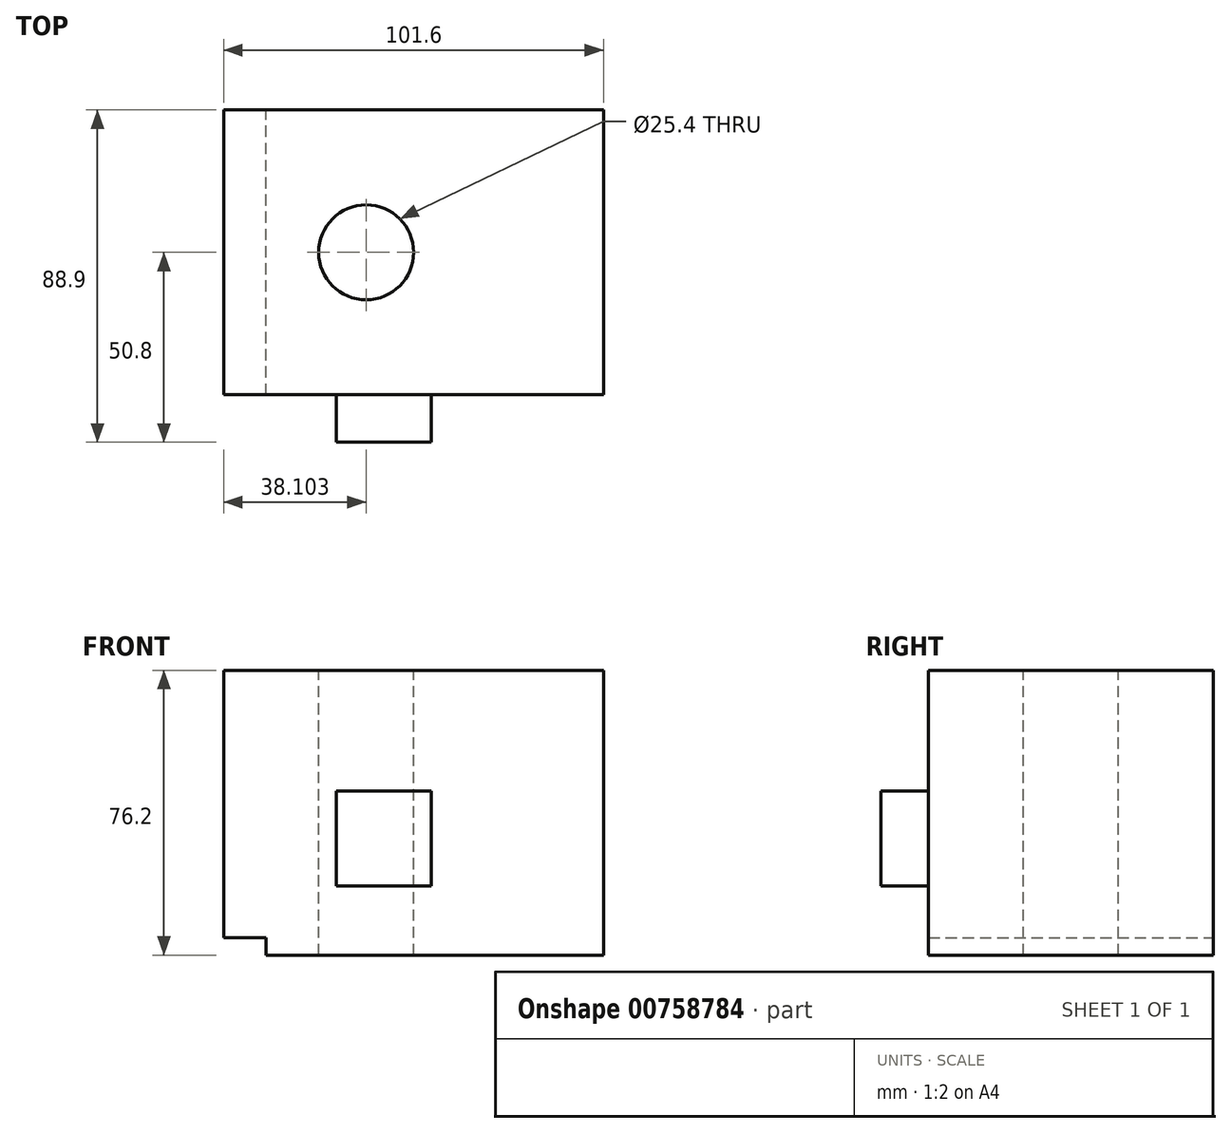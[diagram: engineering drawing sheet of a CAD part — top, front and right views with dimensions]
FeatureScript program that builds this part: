
annotation { "Feature Type Name" : "Feature", "Feature Type Description" : "" }
export const myFeature = defineFeature(function(context is Context, id is Id, definition is map)
    precondition{}
    {
        {
            var Q0;
            Q0=qCreatedBy(makeId("Front.planeOp"),FACE);
            var sketch = newSketch(context, id + "F0", { "sketchPlane" : qUnion([Q0])});
            skLineSegment(sketch, "E0.bottom", {"start": v(-28.32, 14.08) * mm, "end": v(-14.01, 14.08) * mm});
            skLineSegment(sketch, "E0.top", {"start": v(-28.32, 12.85) * mm, "end": v(-14.01, 12.85) * mm});
            skLineSegment(sketch, "E0.left", {"start": v(-28.32, 14.08) * mm, "end": v(-28.32, 12.85) * mm});
            skLineSegment(sketch, "E0.right", {"start": v(-14.01, 14.08) * mm, "end": v(-14.01, 12.85) * mm});
            skLineSegment(sketch, "E1.bottom", {"start": v(-21.17, 12.85) * mm, "end": v(-9.8, 12.85) * mm});
            skLineSegment(sketch, "E1.top", {"start": v(-21.17, 17.5) * mm, "end": v(-9.8, 17.5) * mm});
            skLineSegment(sketch, "E1.left", {"start": v(-21.17, 12.85) * mm, "end": v(-21.17, 17.5) * mm});
            skLineSegment(sketch, "E1.right", {"start": v(-9.8, 12.85) * mm, "end": v(-9.8, 17.5) * mm});
            skLineSegment(sketch, "E2.bottom", {"start": v(-21.17, 12.85) * mm, "end": v(55.03, 12.85) * mm});
            skLineSegment(sketch, "E2.top", {"start": v(-21.17, 89.05) * mm, "end": v(55.03, 89.05) * mm});
            skLineSegment(sketch, "E2.left", {"start": v(-21.17, 12.85) * mm, "end": v(-21.17, 89.05) * mm});
            skLineSegment(sketch, "E2.right", {"start": v(55.03, 12.85) * mm, "end": v(55.03, 89.05) * mm});
            skSolve(sketch);
        }
        {
            var Q0;
            {var subQ4=sQuery(id+"F0.wireOp",EDGE,"E1.top");Q0=makeQuery(id+"F0.imprint","IMPRINT",FACE,{"disambiguationData":[TD([[makeQuery(id+"F0.imprint","IMPRINT",EDGE,{"derivedFrom":subQ4}),1.0]])]});}
            extrude(context, id + "F1", {"entities" : qUnion([Q0]), "depth" : 76.2 * mm, "offsetDistance" : 25.4 * mm});
        }
        {
            var Q0;
            Q0=makeQuery(id+"F1.opExtrude","CAP_FACE",FACE,{"disambiguationData":[OSD([sQuery(id+"F0.wireOp",EDGE,"E1.top"),sQuery(id+"F0.wireOp",EDGE,"E1.right"),sQuery(id+"F0.wireOp",EDGE,"E2.bottom"),sQuery(id+"F0.wireOp",EDGE,"E2.top"),sQuery(id+"F0.wireOp",EDGE,"E2.left"),sQuery(id+"F0.wireOp",EDGE,"E2.right")])],"isStart":false});
            var sketch = newSketch(context, id + "F2", { "sketchPlane" : qUnion([Q0])});
            skLineSegment(sketch, "E3.bottom", {"start": v(9, 56.76) * mm, "end": v(34.4, 56.76) * mm});
            skLineSegment(sketch, "E3.top", {"start": v(9, 31.36) * mm, "end": v(34.4, 31.36) * mm});
            skLineSegment(sketch, "E3.left", {"start": v(9, 56.76) * mm, "end": v(9, 31.36) * mm});
            skLineSegment(sketch, "E3.right", {"start": v(34.4, 56.76) * mm, "end": v(34.4, 31.36) * mm});
            skSolve(sketch);
        }
        {
            var Q0;
            Q0 = qSketchRegion(id + "F2", true);
            extrude(context, id + "F3", {"entities" : qUnion([Q0]), "operationType" : NewBodyOperationType.ADD, "depth" : 12.7 * mm, "offsetDistance" : 25.4 * mm});
        }
        {
            var Q0;
            Q0=makeQuery(id+"F1.opExtrude","SWEPT_FACE",FACE,{"disambiguationData":[OSD([sQuery(id+"F0.wireOp",EDGE,"E2.right")])]});
            var sketch = newSketch(context, id + "F4", { "sketchPlane" : qUnion([Q0])});
            skSolve(sketch);
        }
        {
            var Q0;
            Q0=makeQuery(id+"F1.opExtrude","SWEPT_FACE",FACE,{"disambiguationData":[OSD([sQuery(id+"F0.wireOp",EDGE,"E2.top")])]});
            var sketch = newSketch(context, id + "F5", { "sketchPlane" : qUnion([Q0])});
            skPoint(sketch, "E4", {"position": v(16.93, -38.1) * mm});
            skSolve(sketch);
        }
        {
            var Q0;
            {var subQ0=sQuery(id+"F0.wireOp",EDGE,"E2.right");Q0=makeQuery(id+"F4.imprint","IMPRINT",FACE,{"disambiguationData":[TD([[makeQuery(id+"F4.imprint","IMPRINT",EDGE,{"derivedFrom":makeQuery(id+"F1.opExtrude","CAP_EDGE",EDGE,{"disambiguationData":[OSD([subQ0])],"isStart":true})}),1.0]])]});}
            extrude(context, id + "F6", {"entities" : qUnion([Q0]), "operationType" : NewBodyOperationType.ADD, "depth" : 25.4 * mm, "offsetDistance" : 25.4 * mm});
        }
        {
            var Q0;
            Q0=sQuery(id+"F5.wireOp",VERTEX,"E4");
            var Q1;
            Q1=makeQuery(id+"F1.opExtrude","SWEPT_BODY",BODY,{"disambiguationData":[OSD([sQuery(id+"F0.wireOp",EDGE,"E1.top"),sQuery(id+"F0.wireOp",EDGE,"E1.right"),sQuery(id+"F0.wireOp",EDGE,"E2.bottom"),sQuery(id+"F0.wireOp",EDGE,"E2.top"),sQuery(id+"F0.wireOp",EDGE,"E2.left"),sQuery(id+"F0.wireOp",EDGE,"E2.right")])]});
            hole(context, id + "F7", {"style" : HoleStyle.SIMPLE, "endStyle" : HoleEndStyle.THROUGH, "holeDiameter" : 25.4 * mm, "majorDiameter" : 6.35 * mm, "isTappedThrough" : true, "tappedDepth" : 12.7 * mm, "tapClearance" : 3, "locations" : qUnion([Q0]), "scope" : qUnion([Q1])});
        }
    });
